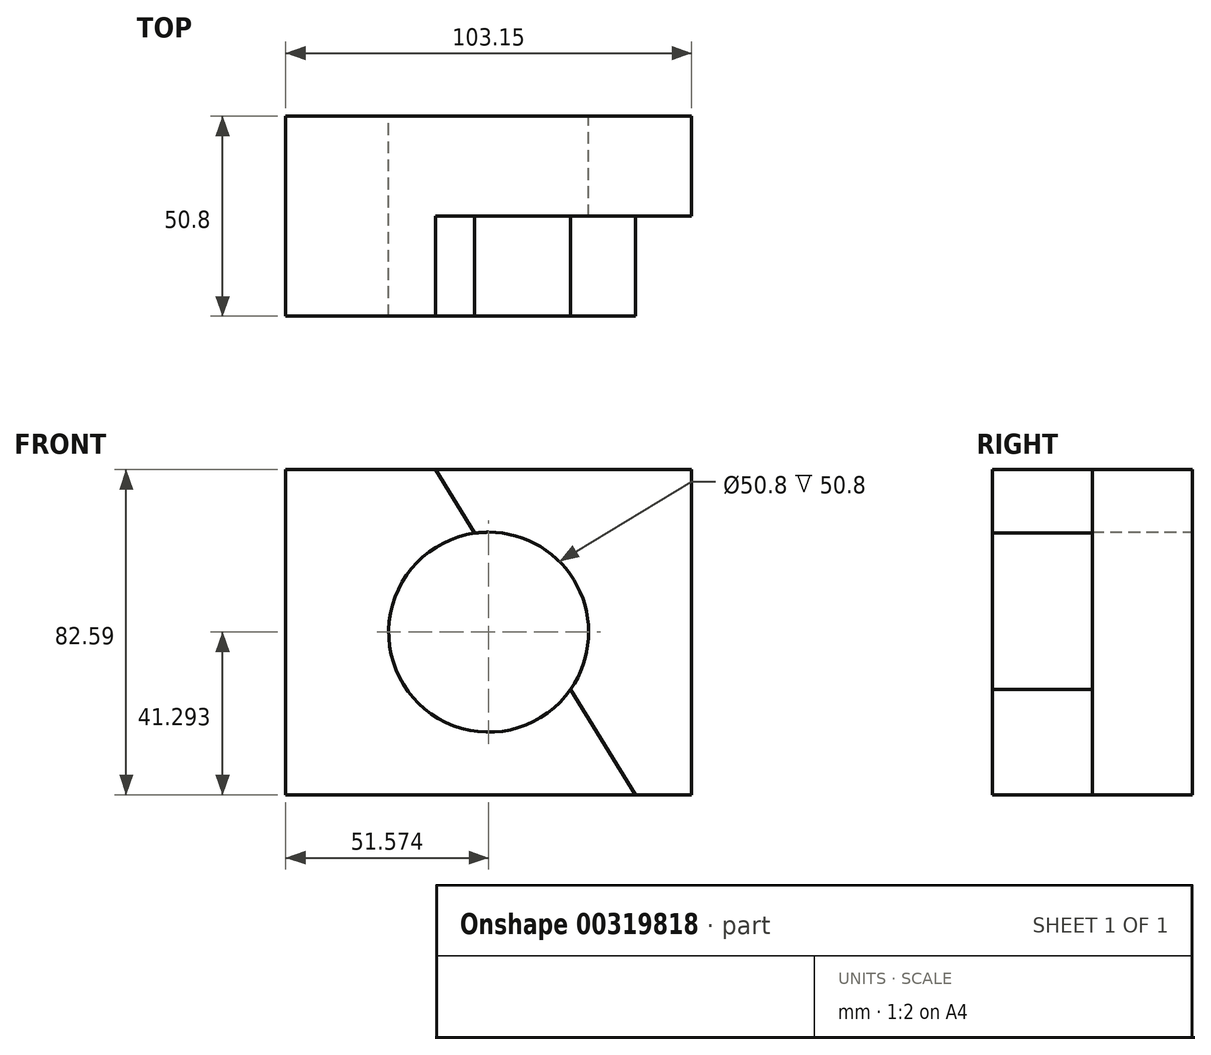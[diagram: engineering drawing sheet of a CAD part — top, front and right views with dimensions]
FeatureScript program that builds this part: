
annotation { "Feature Type Name" : "Feature", "Feature Type Description" : "" }
export const myFeature = defineFeature(function(context is Context, id is Id, definition is map)
    precondition{}
    {
        {
            var Q0;
            Q0=qCreatedBy(makeId("Front.planeOp"),FACE);
            var sketch = newSketch(context, id + "F0", { "sketchPlane" : qUnion([Q0])});
            skLineSegment(sketch, "E0.bottom", {"start": v(-46.78, 32.24) * mm, "end": v(56.37, 32.24) * mm});
            skLineSegment(sketch, "E0.top", {"start": v(-46.78, -50.35) * mm, "end": v(56.37, -50.35) * mm});
            skLineSegment(sketch, "E0.left", {"start": v(-46.78, 32.24) * mm, "end": v(-46.78, -50.35) * mm});
            skLineSegment(sketch, "E0.right", {"start": v(56.37, 32.24) * mm, "end": v(56.37, -50.35) * mm});
            skSolve(sketch);
        }
        {
            var Q0;
            Q0=makeQuery(id+"F0.imprint","IMPRINT",FACE,{"disambiguationData":[TD([[makeQuery(id+"F0.imprint","IMPRINT",EDGE,{"derivedFrom":sQuery(id+"F0.wireOp",EDGE,"E0.bottom")}),-1.0]])]});
            extrude(context, id + "F1", {"entities" : qUnion([Q0]), "oppositeDirection" : true, "depth" : 25.4 * mm});
        }
        {
            var Q0;
            Q0=makeQuery(id+"F1.opExtrude","CAP_FACE",FACE,{"disambiguationData":[OSD([sQuery(id+"F0.wireOp",EDGE,"E0.bottom"),sQuery(id+"F0.wireOp",EDGE,"E0.top"),sQuery(id+"F0.wireOp",EDGE,"E0.left"),sQuery(id+"F0.wireOp",EDGE,"E0.right")])],"isStart":true});
            var sketch = newSketch(context, id + "F2", { "sketchPlane" : qUnion([Q0])});
            skLineSegment(sketch, "E1", {"start": v(-46.78, 32.24) * mm, "end": v(-8.68, 32.24) * mm});
            skLineSegment(sketch, "E2", {"start": v(-8.68, 32.24) * mm, "end": v(42.12, -50.35) * mm});
            skLineSegment(sketch, "E3", {"start": v(42.12, -50.35) * mm, "end": v(-46.78, -50.35) * mm});
            skLineSegment(sketch, "E4", {"start": v(-46.78, -50.35) * mm, "end": v(-46.78, 32.24) * mm});
            skSolve(sketch);
        }
        {
            var Q0;
            Q0=makeQuery(id+"F2.imprint","IMPRINT",FACE,{"disambiguationData":[TD([[makeQuery(id+"F2.imprint","IMPRINT",EDGE,{"derivedFrom":sQuery(id+"F2.wireOp",EDGE,"E1")}),-1.0]])]});
            extrude(context, id + "F3", {"entities" : qUnion([Q0]), "operationType" : NewBodyOperationType.ADD, "depth" : 25.4 * mm});
        }
        {
            var Q0;
            Q0=makeQuery(id+"F1.opExtrude","CAP_FACE",FACE,{"disambiguationData":[OSD([sQuery(id+"F0.wireOp",EDGE,"E0.bottom"),sQuery(id+"F0.wireOp",EDGE,"E0.top"),sQuery(id+"F0.wireOp",EDGE,"E0.left"),sQuery(id+"F0.wireOp",EDGE,"E0.right")])],"isStart":false});
            var sketch = newSketch(context, id + "F4", { "sketchPlane" : qUnion([Q0])});
            skCircle(sketch, "E5", {"center": v(-4.8, -9.06) * mm, "radius": 25.4 * mm});
            skPoint(sketch, "E5.centerSnap0", {"position": v(46.78, -9.06) * mm});
            skPoint(sketch, "E5.centerSnap1", {"position": v(-4.8, 32.24) * mm});
            skSolve(sketch);
        }
        {
            var Q0;
            Q0=makeQuery(id+"F4.imprint","IMPRINT",FACE,{"disambiguationData":[TD([[makeQuery(id+"F4.imprint","IMPRINT",EDGE,{"derivedFrom":sQuery(id+"F4.wireOp",EDGE,"E5")}),1.0]])]});
            extrude(context, id + "F5", {"entities" : qUnion([Q0]), "operationType" : NewBodyOperationType.REMOVE, "oppositeDirection" : true, "depth" : 127 * mm});
        }
    });
